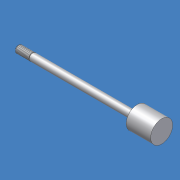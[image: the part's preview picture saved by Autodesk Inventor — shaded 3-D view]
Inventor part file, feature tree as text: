
AUTODESK INVENTOR PART (.ipt)
format: ipt  version: 2012 (Build 160160000, 160)  size: 128,512 bytes
history: native  units: mm (DEFAULTED — no unit token found)
features: other x84, revolve x3, sketch x3, thread x1
ambient origin geometry x8: Origin, YZ Plane, XZ Plane, XY Plane, X Axis, Y Axis, Z Axis, Center Point
bodies: Solid1 (feature_tree)
feature tree (91):
  revolve  "Revolution1"  Angle=360.0deg
  revolve  "Revolution2"  Angle=360.0deg
  thread  "Thread1"  [1 undecoded]
  revolve  "Revolution3"  [1 undecoded]
  other  "rod_cp_XY"
  other  "rod_cp_YZ"
  other  "rod_cp_ZX"
  other  "rod_cp_X"
  other  "rod_cp_Y"
  other  "rod_cp_Z"
  other  "rod_cp_Center"
  other  "to_rod_clevis_XY"
  other  "to_rod_clevis_YZ"
  other  "to_rod_clevis_ZX"
  other  "to_rod_clevis_X"
  other  "to_rod_clevis_Y"
  other  "to_rod_clevis_Z"
  other  "to_rod_clevis_Center"
  other  "rl2_XY"
  other  "rl2_YZ"
  other  "rl2_ZX"
  other  "rl2_X"
  other  "rl2_Y"
  other  "rl2_Z"
  other  "rl2_Center"
  other  "rl1_XY"
  other  "rl1_YZ"
  other  "rl1_ZX"
  other  "rl1_X"
  other  "rl1_Y"
  other  "rl1_Z"
  other  "rl1_Center"
  other  "thd1_XY"
  other  "thd1_YZ"
  other  "thd1_ZX"
  other  "thd1_X"
  other  "thd1_Y"
  other  "thd1_Z"
  other  "thd1_Center"
  other  "thd2_XY"
  other  "thd2_YZ"
  other  "thd2_ZX"
  other  "thd2_X"
  other  "thd2_Y"
  other  "thd2_Z"
  other  "thd2_Center"
  other  "dia1_XY"
  other  "dia1_YZ"
  other  "dia1_ZX"
  other  "dia1_X"
  other  "dia1_Y"
  other  "dia1_Z"
  other  "dia1_Center"
  other  "dia2_XY"
  other  "dia2_YZ"
  other  "dia2_ZX"
  other  "dia2_X"
  other  "dia2_Y"
  other  "dia2_Z"
  other  "dia2_Center"
  other  "hh1_XY"
  other  "hh1_YZ"
  other  "hh1_ZX"
  other  "hh1_X"
  other  "hh1_Y"
  other  "hh1_Z"
  other  "hh1_Center"
  other  "hh2_XY"
  other  "hh2_YZ"
  other  "hh2_ZX"
  other  "hh2_X"
  other  "hh2_Y"
  other  "hh2_Z"
  other  "hh2_Center"
  other  "dia12_XY"
  other  "dia12_YZ"
  other  "dia12_ZX"
  other  "dia12_X"
  other  "dia12_Y"
  other  "dia12_Z"
  other  "dia12_Center"
  other  "dia22_XY"
  other  "dia22_YZ"
  other  "dia22_ZX"
  other  "dia22_X"
  other  "dia22_Y"
  other  "dia22_Z"
  other  "dia22_Center"
  sketch  "Sketch_1"  dims[d0=360.0deg d1=360.0deg]
  sketch  "Sketch_3"  dims[d2=12.7mm d3=91.2876mm d4=360.0deg]
  sketch  "Sketch_30"
note: 2 required parameter values undecoded (feature->parameter linkage not recoverable at this tier; creation-order binding heuristic only, values carry confidence <= 0.55)
